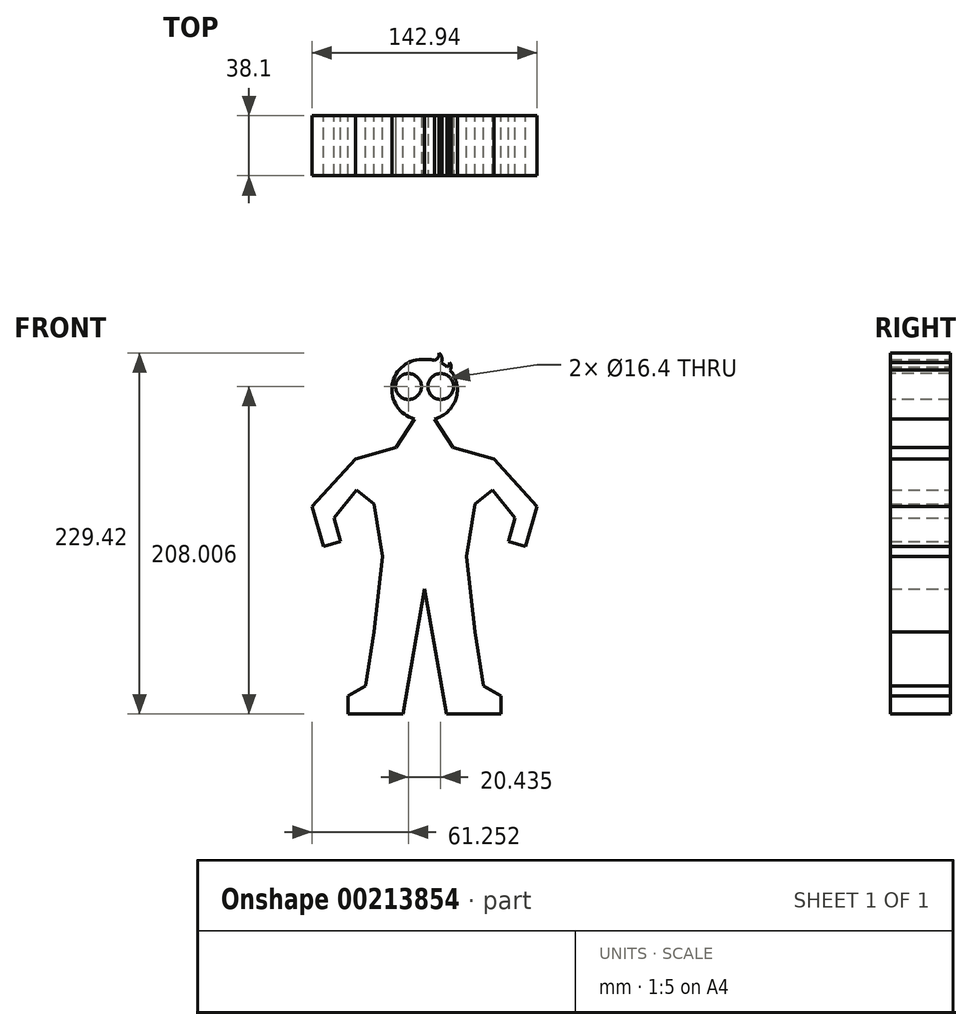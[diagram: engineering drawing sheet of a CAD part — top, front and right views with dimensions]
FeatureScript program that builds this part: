
annotation { "Feature Type Name" : "Feature", "Feature Type Description" : "" }
export const myFeature = defineFeature(function(context is Context, id is Id, definition is map)
    precondition{}
    {
        {
            var Q0;
            Q0=qCreatedBy(makeId("Front.planeOp"),FACE);
            var sketch = newSketch(context, id + "F0", { "sketchPlane" : qUnion([Q0])});
            skLineSegment(sketch, "E0", {"start": v(-26.64, 0) * mm, "end": v(-32.14, 33.16) * mm});
            skLineSegment(sketch, "E1", {"start": v(-32.14, 33.16) * mm, "end": v(-43.14, 42.04) * mm});
            skLineSegment(sketch, "E2", {"start": v(-43.14, 42.04) * mm, "end": v(-57.54, 24.2) * mm});
            skLineSegment(sketch, "E3", {"start": v(-57.54, 24.2) * mm, "end": v(-53.29, 9.47) * mm});
            skLineSegment(sketch, "E4", {"start": v(-53.29, 9.47) * mm, "end": v(-64.17, 6.33) * mm});
            skLineSegment(sketch, "E5", {"start": v(-64.17, 6.33) * mm, "end": v(-71.47, 31.59) * mm});
            skLineSegment(sketch, "E6", {"start": v(-71.47, 31.59) * mm, "end": v(-43.98, 61.91) * mm});
            skLineSegment(sketch, "E7", {"start": v(-43.98, 61.91) * mm, "end": v(-18.19, 69.1) * mm});
            skLineSegment(sketch, "E8", {"start": v(-18.19, 69.1) * mm, "end": v(-6.35, 87.29) * mm});
            skArc(sketch, "E9", {"start": v(0, 124.92) * mm, "mid": v(-20.56, 109.04) * mm, "end": v(-6.35, 87.29) * mm});
            skLineSegment(sketch, "E10", {"start": v(-26.64, 0) * mm, "end": v(-32.14, -48.04) * mm});
            skLineSegment(sketch, "E11", {"start": v(-32.14, -48.04) * mm, "end": v(-37.48, -82.2) * mm});
            skLineSegment(sketch, "E12", {"start": v(-37.48, -82.2) * mm, "end": v(-48.5, -88.6) * mm});
            skLineSegment(sketch, "E13", {"start": v(-48.5, -88.6) * mm, "end": v(-48.5, -100.2) * mm});
            skLineSegment(sketch, "E14", {"start": v(-48.5, -100.2) * mm, "end": v(-13.84, -100.2) * mm});
            skLineSegment(sketch, "E15", {"start": v(-13.84, -100.2) * mm, "end": v(0, -20.61) * mm});
            skLineSegment(sketch, "E16", {"start": v(0, -20.61) * mm, "end": v(0, 124.92) * mm});
            skLineSegment(sketch, "E17", {"start": v(0, 124.92) * mm, "end": v(0, -20.61) * mm, "construction": true});
            skLineSegment(sketch, "E18.MirrorCS", {"start": v(32.14, 33.16) * mm, "end": v(43.14, 42.04) * mm});
            skLineSegment(sketch, "E19.MirrorCS", {"start": v(37.48, -82.2) * mm, "end": v(48.5, -88.6) * mm});
            skLineSegment(sketch, "E20.MirrorCS", {"start": v(48.5, -88.6) * mm, "end": v(48.5, -100.2) * mm});
            skLineSegment(sketch, "E21.MirrorCS", {"start": v(53.29, 9.47) * mm, "end": v(64.17, 6.33) * mm});
            skLineSegment(sketch, "E22.MirrorCS", {"start": v(26.64, 0) * mm, "end": v(32.14, 33.16) * mm});
            skLineSegment(sketch, "E23.MirrorCS", {"start": v(13.84, -100.2) * mm, "end": v(0, -20.61) * mm});
            skLineSegment(sketch, "E24.MirrorCS", {"start": v(48.5, -100.2) * mm, "end": v(13.84, -100.2) * mm});
            skLineSegment(sketch, "E25.MirrorCS", {"start": v(32.14, -48.04) * mm, "end": v(37.48, -82.2) * mm});
            skLineSegment(sketch, "E26.MirrorCS", {"start": v(43.14, 42.04) * mm, "end": v(57.54, 24.2) * mm});
            skLineSegment(sketch, "E27.MirrorCS", {"start": v(26.64, 0) * mm, "end": v(32.14, -48.04) * mm});
            skArc(sketch, "E28.MirrorCS", {"start": v(0, 124.92) * mm, "mid": v(20.56, 109.04) * mm, "end": v(6.35, 87.29) * mm});
            skLineSegment(sketch, "E29.MirrorCS", {"start": v(57.54, 24.2) * mm, "end": v(53.29, 9.47) * mm});
            skLineSegment(sketch, "E30.MirrorCS", {"start": v(43.98, 61.91) * mm, "end": v(18.19, 69.1) * mm});
            skLineSegment(sketch, "E31.MirrorCS", {"start": v(64.17, 6.33) * mm, "end": v(71.47, 31.59) * mm});
            skLineSegment(sketch, "E32.MirrorCS", {"start": v(18.19, 69.1) * mm, "end": v(6.35, 87.29) * mm});
            skLineSegment(sketch, "E33.MirrorCS", {"start": v(71.47, 31.59) * mm, "end": v(43.98, 61.91) * mm});
            skSolve(sketch);
        }
        {
            var Q0;
            Q0=makeQuery(id+"F0.imprint","IMPRINT",FACE,{"disambiguationData":[TD([[makeQuery(id+"F0.imprint","IMPRINT",EDGE,{"derivedFrom":sQuery(id+"F0.wireOp",EDGE,"E0")}),-1.0]])]});
            var Q1;
            Q1=makeQuery(id+"F0.imprint","IMPRINT",FACE,{"disambiguationData":[TD([[makeQuery(id+"F0.imprint","IMPRINT",EDGE,{"derivedFrom":sQuery(id+"F0.wireOp",EDGE,"E16")}),-1.0]])]});
            extrude(context, id + "F1", {"entities" : qUnion([Q0, Q1]), "endBound" : BoundingType.SYMMETRIC, "depth" : 38.1 * mm});
        }
        {
            var Q0;
            Q0=makeQuery(id+"F1.opExtrude","CAP_FACE",FACE,{"disambiguationData":[OSD([sQuery(id+"F0.wireOp",EDGE,"E0"),sQuery(id+"F0.wireOp",EDGE,"E1"),sQuery(id+"F0.wireOp",EDGE,"E2"),sQuery(id+"F0.wireOp",EDGE,"E3"),sQuery(id+"F0.wireOp",EDGE,"E4"),sQuery(id+"F0.wireOp",EDGE,"E5"),sQuery(id+"F0.wireOp",EDGE,"E6"),sQuery(id+"F0.wireOp",EDGE,"E7"),sQuery(id+"F0.wireOp",EDGE,"E8"),sQuery(id+"F0.wireOp",EDGE,"E9"),sQuery(id+"F0.wireOp",EDGE,"E10"),sQuery(id+"F0.wireOp",EDGE,"E11"),sQuery(id+"F0.wireOp",EDGE,"E12"),sQuery(id+"F0.wireOp",EDGE,"E13"),sQuery(id+"F0.wireOp",EDGE,"E14"),sQuery(id+"F0.wireOp",EDGE,"E15"),sQuery(id+"F0.wireOp",EDGE,"E18.MirrorCS"),sQuery(id+"F0.wireOp",EDGE,"E19.MirrorCS"),sQuery(id+"F0.wireOp",EDGE,"E20.MirrorCS"),sQuery(id+"F0.wireOp",EDGE,"E21.MirrorCS"),sQuery(id+"F0.wireOp",EDGE,"E22.MirrorCS"),sQuery(id+"F0.wireOp",EDGE,"E23.MirrorCS"),sQuery(id+"F0.wireOp",EDGE,"E24.MirrorCS"),sQuery(id+"F0.wireOp",EDGE,"E25.MirrorCS"),sQuery(id+"F0.wireOp",EDGE,"E26.MirrorCS"),sQuery(id+"F0.wireOp",EDGE,"E27.MirrorCS"),sQuery(id+"F0.wireOp",EDGE,"E28.MirrorCS"),sQuery(id+"F0.wireOp",EDGE,"E29.MirrorCS"),sQuery(id+"F0.wireOp",EDGE,"E30.MirrorCS"),sQuery(id+"F0.wireOp",EDGE,"E31.MirrorCS"),sQuery(id+"F0.wireOp",EDGE,"E32.MirrorCS"),sQuery(id+"F0.wireOp",EDGE,"E33.MirrorCS")])],"isStart":false});
            var sketch = newSketch(context, id + "F2", { "sketchPlane" : qUnion([Q0])});
            skCircle(sketch, "E34", {"center": v(-10.22, 107.8) * mm, "radius": 8.2 * mm});
            skLineSegment(sketch, "E35", {"start": v(0, 124.92) * mm, "end": v(0, 0) * mm, "construction": true});
            skCircle(sketch, "E36.MirrorC", {"center": v(10.22, 107.8) * mm, "radius": 8.2 * mm});
            skSolve(sketch);
        }
        {
            var Q0;
            Q0 = qSketchRegion(id + "F2", true);
            extrude(context, id + "F3", {"entities" : qUnion([Q0]), "operationType" : NewBodyOperationType.REMOVE, "endBound" : BoundingType.UP_TO_NEXT, "oppositeDirection" : true, "depth" : 25.4 * mm, "hasSecondDirection" : true, "secondDirectionOppositeDirection" : false, "secondDirectionDepth" : 25.4 * mm});
        }
        {
            var Q0;
            Q0=makeQuery(id+"F1.opExtrude","CAP_FACE",FACE,{"disambiguationData":[OSD([sQuery(id+"F0.wireOp",EDGE,"E0"),sQuery(id+"F0.wireOp",EDGE,"E1"),sQuery(id+"F0.wireOp",EDGE,"E2"),sQuery(id+"F0.wireOp",EDGE,"E3"),sQuery(id+"F0.wireOp",EDGE,"E4"),sQuery(id+"F0.wireOp",EDGE,"E5"),sQuery(id+"F0.wireOp",EDGE,"E6"),sQuery(id+"F0.wireOp",EDGE,"E7"),sQuery(id+"F0.wireOp",EDGE,"E8"),sQuery(id+"F0.wireOp",EDGE,"E9"),sQuery(id+"F0.wireOp",EDGE,"E10"),sQuery(id+"F0.wireOp",EDGE,"E11"),sQuery(id+"F0.wireOp",EDGE,"E12"),sQuery(id+"F0.wireOp",EDGE,"E13"),sQuery(id+"F0.wireOp",EDGE,"E14"),sQuery(id+"F0.wireOp",EDGE,"E15"),sQuery(id+"F0.wireOp",EDGE,"E18.MirrorCS"),sQuery(id+"F0.wireOp",EDGE,"E19.MirrorCS"),sQuery(id+"F0.wireOp",EDGE,"E20.MirrorCS"),sQuery(id+"F0.wireOp",EDGE,"E21.MirrorCS"),sQuery(id+"F0.wireOp",EDGE,"E22.MirrorCS"),sQuery(id+"F0.wireOp",EDGE,"E23.MirrorCS"),sQuery(id+"F0.wireOp",EDGE,"E24.MirrorCS"),sQuery(id+"F0.wireOp",EDGE,"E25.MirrorCS"),sQuery(id+"F0.wireOp",EDGE,"E26.MirrorCS"),sQuery(id+"F0.wireOp",EDGE,"E27.MirrorCS"),sQuery(id+"F0.wireOp",EDGE,"E28.MirrorCS"),sQuery(id+"F0.wireOp",EDGE,"E29.MirrorCS"),sQuery(id+"F0.wireOp",EDGE,"E30.MirrorCS"),sQuery(id+"F0.wireOp",EDGE,"E31.MirrorCS"),sQuery(id+"F0.wireOp",EDGE,"E32.MirrorCS"),sQuery(id+"F0.wireOp",EDGE,"E33.MirrorCS")])],"isStart":true});
            var sketch = newSketch(context, id + "F4", { "sketchPlane" : qUnion([Q0])});
            skLineSegment(sketch, "E37", {"start": v(0, 124.92) * mm, "end": v(0, 0) * mm, "construction": true});
            skArc(sketch, "E38", {"start": v(-9.1, 129.21) * mm, "mid": v(-8.55, 126.27) * mm, "end": v(-6.16, 124.47) * mm});
            skArc(sketch, "E39", {"start": v(-9.1, 129.21) * mm, "mid": v(-10.94, 126.3) * mm, "end": v(-10.44, 122.88) * mm});
            skArc(sketch, "E40", {"start": v(-15.75, 123.2) * mm, "mid": v(-15.5, 121.49) * mm, "end": v(-14.27, 120.28) * mm});
            skArc(sketch, "E41", {"start": v(-15.75, 123.2) * mm, "mid": v(-16.9, 120.88) * mm, "end": v(-16.14, 118.41) * mm});
            skArc(sketch, "E42.MirrorCS", {"start": v(15.75, 123.2) * mm, "mid": v(15.5, 121.49) * mm, "end": v(14.27, 120.28) * mm});
            skArc(sketch, "E43.MirrorCS", {"start": v(9.1, 129.21) * mm, "mid": v(8.55, 126.27) * mm, "end": v(6.16, 124.47) * mm});
            skArc(sketch, "E44.MirrorCS", {"start": v(15.75, 123.2) * mm, "mid": v(16.9, 120.88) * mm, "end": v(16.14, 118.41) * mm});
            skArc(sketch, "E45.MirrorCS", {"start": v(9.1, 129.21) * mm, "mid": v(10.94, 126.3) * mm, "end": v(10.44, 122.88) * mm});
            skSolve(sketch);
        }
        {
            var Q0;
            {var subQ0=sQuery(id+"F4.wireOp",EDGE,"E38");Q0=makeQuery(id+"F4.imprint","IMPRINT",FACE,{"disambiguationData":[TD([[makeQuery(id+"F4.imprint","IMPRINT",EDGE,{"derivedFrom":subQ0}),-1.0]])]});}
            var Q1;
            {var subQ0=sQuery(id+"F4.wireOp",EDGE,"E40");Q1=makeQuery(id+"F4.imprint","IMPRINT",FACE,{"disambiguationData":[TD([[makeQuery(id+"F4.imprint","IMPRINT",EDGE,{"derivedFrom":subQ0}),-1.0]])]});}
            var Q2;
            {var subQ0=sQuery(id+"F4.wireOp",EDGE,"E43.MirrorCS");Q2=makeQuery(id+"F4.imprint","IMPRINT",FACE,{"disambiguationData":[TD([[makeQuery(id+"F4.imprint","IMPRINT",EDGE,{"derivedFrom":subQ0}),1.0]])]});}
            var Q3;
            {var subQ0=sQuery(id+"F4.wireOp",EDGE,"E42.MirrorCS");Q3=makeQuery(id+"F4.imprint","IMPRINT",FACE,{"disambiguationData":[TD([[makeQuery(id+"F4.imprint","IMPRINT",EDGE,{"derivedFrom":subQ0}),1.0]])]});}
            var Q4;
            Q4=makeQuery(id+"F1.opExtrude","CAP_FACE",FACE,{"disambiguationData":[OSD([sQuery(id+"F0.wireOp",EDGE,"E0"),sQuery(id+"F0.wireOp",EDGE,"E1"),sQuery(id+"F0.wireOp",EDGE,"E2"),sQuery(id+"F0.wireOp",EDGE,"E3"),sQuery(id+"F0.wireOp",EDGE,"E4"),sQuery(id+"F0.wireOp",EDGE,"E5"),sQuery(id+"F0.wireOp",EDGE,"E6"),sQuery(id+"F0.wireOp",EDGE,"E7"),sQuery(id+"F0.wireOp",EDGE,"E8"),sQuery(id+"F0.wireOp",EDGE,"E9"),sQuery(id+"F0.wireOp",EDGE,"E10"),sQuery(id+"F0.wireOp",EDGE,"E11"),sQuery(id+"F0.wireOp",EDGE,"E12"),sQuery(id+"F0.wireOp",EDGE,"E13"),sQuery(id+"F0.wireOp",EDGE,"E14"),sQuery(id+"F0.wireOp",EDGE,"E15"),sQuery(id+"F0.wireOp",EDGE,"E18.MirrorCS"),sQuery(id+"F0.wireOp",EDGE,"E19.MirrorCS"),sQuery(id+"F0.wireOp",EDGE,"E20.MirrorCS"),sQuery(id+"F0.wireOp",EDGE,"E21.MirrorCS"),sQuery(id+"F0.wireOp",EDGE,"E22.MirrorCS"),sQuery(id+"F0.wireOp",EDGE,"E23.MirrorCS"),sQuery(id+"F0.wireOp",EDGE,"E24.MirrorCS"),sQuery(id+"F0.wireOp",EDGE,"E25.MirrorCS"),sQuery(id+"F0.wireOp",EDGE,"E26.MirrorCS"),sQuery(id+"F0.wireOp",EDGE,"E27.MirrorCS"),sQuery(id+"F0.wireOp",EDGE,"E28.MirrorCS"),sQuery(id+"F0.wireOp",EDGE,"E29.MirrorCS"),sQuery(id+"F0.wireOp",EDGE,"E30.MirrorCS"),sQuery(id+"F0.wireOp",EDGE,"E31.MirrorCS"),sQuery(id+"F0.wireOp",EDGE,"E32.MirrorCS"),sQuery(id+"F0.wireOp",EDGE,"E33.MirrorCS")])],"isStart":false});
            var Q5;
            Q5=makeQuery(id+"F1.opExtrude","SWEPT_BODY",BODY,{"disambiguationData":[OSD([sQuery(id+"F0.wireOp",EDGE,"E0"),sQuery(id+"F0.wireOp",EDGE,"E1"),sQuery(id+"F0.wireOp",EDGE,"E2"),sQuery(id+"F0.wireOp",EDGE,"E3"),sQuery(id+"F0.wireOp",EDGE,"E4"),sQuery(id+"F0.wireOp",EDGE,"E5"),sQuery(id+"F0.wireOp",EDGE,"E6"),sQuery(id+"F0.wireOp",EDGE,"E7"),sQuery(id+"F0.wireOp",EDGE,"E8"),sQuery(id+"F0.wireOp",EDGE,"E9"),sQuery(id+"F0.wireOp",EDGE,"E10"),sQuery(id+"F0.wireOp",EDGE,"E11"),sQuery(id+"F0.wireOp",EDGE,"E12"),sQuery(id+"F0.wireOp",EDGE,"E13"),sQuery(id+"F0.wireOp",EDGE,"E14"),sQuery(id+"F0.wireOp",EDGE,"E15"),sQuery(id+"F0.wireOp",EDGE,"E18.MirrorCS"),sQuery(id+"F0.wireOp",EDGE,"E19.MirrorCS"),sQuery(id+"F0.wireOp",EDGE,"E20.MirrorCS"),sQuery(id+"F0.wireOp",EDGE,"E21.MirrorCS"),sQuery(id+"F0.wireOp",EDGE,"E22.MirrorCS"),sQuery(id+"F0.wireOp",EDGE,"E23.MirrorCS"),sQuery(id+"F0.wireOp",EDGE,"E24.MirrorCS"),sQuery(id+"F0.wireOp",EDGE,"E25.MirrorCS"),sQuery(id+"F0.wireOp",EDGE,"E26.MirrorCS"),sQuery(id+"F0.wireOp",EDGE,"E27.MirrorCS"),sQuery(id+"F0.wireOp",EDGE,"E28.MirrorCS"),sQuery(id+"F0.wireOp",EDGE,"E29.MirrorCS"),sQuery(id+"F0.wireOp",EDGE,"E30.MirrorCS"),sQuery(id+"F0.wireOp",EDGE,"E31.MirrorCS"),sQuery(id+"F0.wireOp",EDGE,"E32.MirrorCS"),sQuery(id+"F0.wireOp",EDGE,"E33.MirrorCS")])]});
            extrude(context, id + "F5", {"entities" : qUnion([Q0, Q1, Q2, Q3]), "operationType" : NewBodyOperationType.ADD, "endBound" : BoundingType.UP_TO_SURFACE, "oppositeDirection" : true, "endBoundEntityFace" : qUnion([Q4]), "endBoundEntityBody" : qUnion([Q5]), "depth" : 25.4 * mm});
        }
    });
